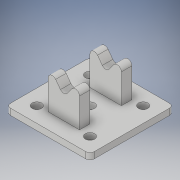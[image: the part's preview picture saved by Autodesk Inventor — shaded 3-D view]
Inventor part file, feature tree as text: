
AUTODESK INVENTOR PART (.ipt)
format: ipt  version: 2019 (Build 230136000, 136)  size: 168,960 bytes
history: native  units: in
note: dims shown in document units (in); Inventor stores cm internally (conversion verified against a paired STEP export)
features: sketch x4, extrude x3, fillet x1, hole x1
ambient origin geometry x8: Origin, YZ Plane, XZ Plane, XY Plane, X Axis, Y Axis, Z Axis, Center Point
bodies: Solid1 (feature_tree)
feature tree (9):
  extrude  "Extrusion1"  Depth=1.5748in
  extrude  "Extrusion2"  Depth=0.7874in TaperAngle=0.0deg
  extrude  "Extrusion3"  Depth=0.0787in
  fillet  "Fillet1"  Radius=0.5906in
  hole  "Hole1"  [1 undecoded]
  sketch  "Sketch1"  dims[d0=1.5748in d1=1.5748in]
  sketch  "Sketch2"  dims[d2=0.1181in d3=0.0in d5=0.7874in d6=0.0in]
  sketch  "Sketch3"  dims[d7=0.7874in d8=0.0in d9=0.0787in d10=0.5906in]
  sketch  "Sketch5"  dims[d11=0.5906in d12=0.1969in d13=0.3937in d14=1.0in d15=1.0in d16=0.177in d17=0.276in d18=0.332in d19=0.0787in d20=0.5635in d21=0.315in d22=0.8108in]
note: 1 required parameter value undecoded (feature->parameter linkage not recoverable at this tier; creation-order binding heuristic only, values carry confidence <= 0.55)
